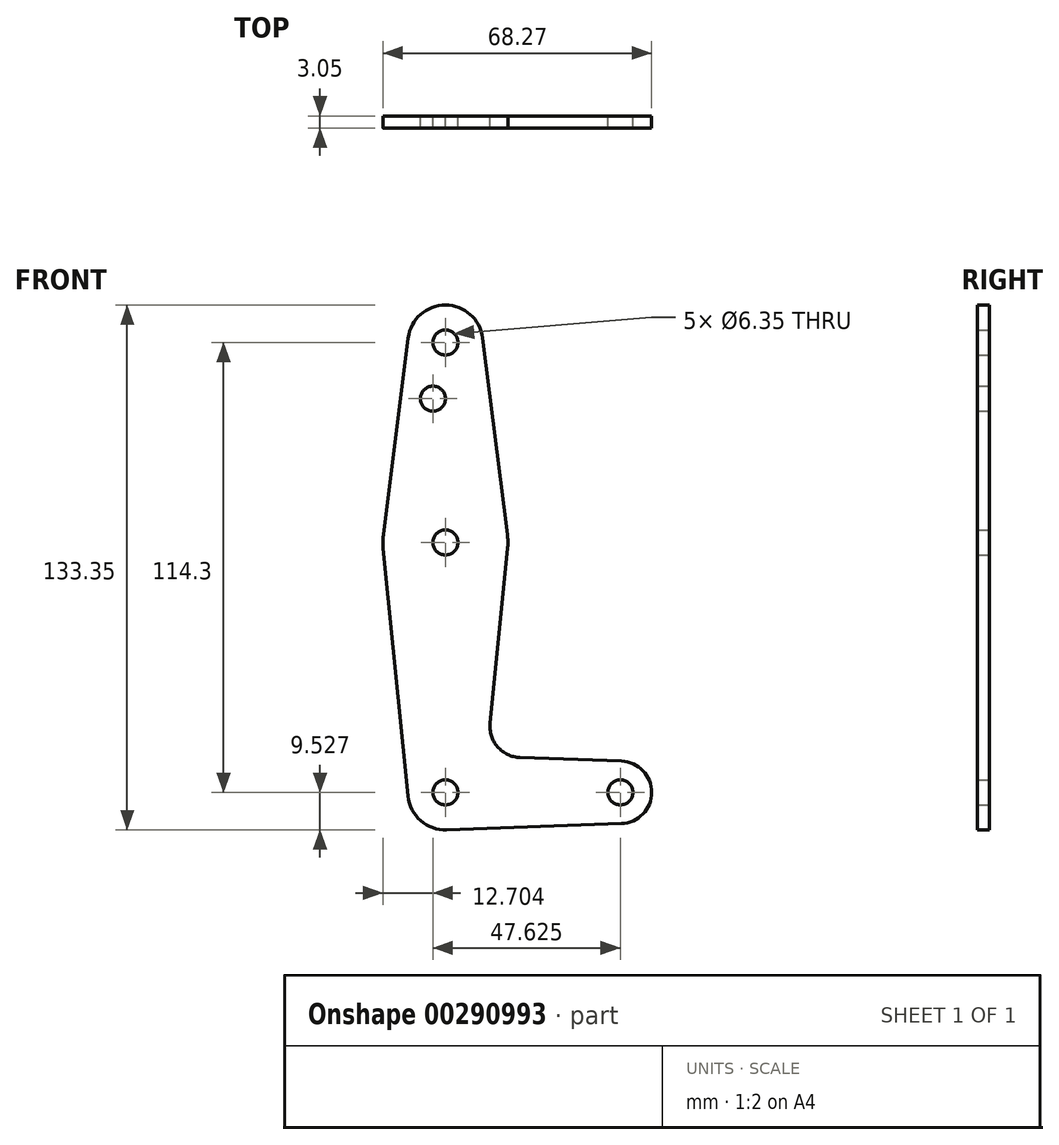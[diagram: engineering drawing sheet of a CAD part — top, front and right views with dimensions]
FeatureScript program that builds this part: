
annotation { "Feature Type Name" : "Feature", "Feature Type Description" : "" }
export const myFeature = defineFeature(function(context is Context, id is Id, definition is map)
    precondition{}
    {
        {
            var Q0;
            Q0=qCreatedBy(makeId("Front.planeOp"),FACE);
            var sketch = newSketch(context, id + "F0", { "sketchPlane" : qUnion([Q0])});
            skLineSegment(sketch, "E0", {"start": v(-31.57, 52.39) * mm, "end": v(-31.57, -61.91) * mm, "construction": true});
            skLineSegment(sketch, "E1", {"start": v(12.88, -61.91) * mm, "end": v(-31.57, -61.91) * mm});
            skCircle(sketch, "E2", {"center": v(-31.57, 52.39) * mm, "radius": 9.53 * mm});
            skCircle(sketch, "E3", {"center": v(-31.57, 1.59) * mm, "radius": 15.88 * mm});
            skCircle(sketch, "E4", {"center": v(-31.57, -61.91) * mm, "radius": 9.53 * mm});
            skCircle(sketch, "E5", {"center": v(12.88, -61.91) * mm, "radius": 7.94 * mm});
            skLineSegment(sketch, "E6", {"start": v(-47.32, 3.57) * mm, "end": v(-41.02, 53.58) * mm});
            skLineSegment(sketch, "E7", {"start": v(-15.82, 3.57) * mm, "end": v(-22.12, 53.58) * mm});
            skLineSegment(sketch, "E8", {"start": v(-47.37, 0) * mm, "end": v(-41.05, -62.87) * mm});
            skLineSegment(sketch, "E9", {"start": v(-15.78, 0) * mm, "end": v(-20.23, -44.32) * mm});
            skLineSegment(sketch, "E10", {"start": v(-12.6, -53.06) * mm, "end": v(13.16, -53.98) * mm});
            skLineSegment(sketch, "E11", {"start": v(13.16, -69.84) * mm, "end": v(-31.57, -71.44) * mm});
            skCircle(sketch, "E12", {"center": v(-31.57, 52.39) * mm, "radius": 3.18 * mm});
            skCircle(sketch, "E13", {"center": v(-34.75, 38.11) * mm, "radius": 3.18 * mm});
            skCircle(sketch, "E14", {"center": v(-31.57, 1.59) * mm, "radius": 3.18 * mm});
            skCircle(sketch, "E15", {"center": v(-31.57, -61.91) * mm, "radius": 3.18 * mm});
            skCircle(sketch, "E16", {"center": v(12.88, -61.91) * mm, "radius": 3.18 * mm});
            skPoint(sketch, "E17.newPointB", {"position": v(-31.57, -52.39) * mm});
            skArc(sketch, "E17.filletArc", {"start": v(-20.23, -44.32) * mm, "mid": v(-18.3, -50.35) * mm, "end": v(-12.6, -53.06) * mm});
            skSolve(sketch);
        }
        {
            var Q0;
            {var subQ1=sQuery(id+"F0.wireOp",EDGE,"E6");Q0=makeQuery(id+"F0.imprint","IMPRINT",FACE,{"disambiguationData":[TD([[makeQuery(id+"F0.imprint","IMPRINT",EDGE,{"derivedFrom":subQ1}),-1.0]])]});}
            var Q1;
            Q1=makeQuery(id+"F0.imprint","IMPRINT",FACE,{"disambiguationData":[TD([[makeQuery(id+"F0.imprint","IMPRINT",EDGE,{"derivedFrom":sQuery(id+"F0.wireOp",EDGE,"E12")}),-1.0]])]});
            var Q2;
            Q2=makeQuery(id+"F0.imprint","IMPRINT",FACE,{"disambiguationData":[TD([[makeQuery(id+"F0.imprint","IMPRINT",EDGE,{"derivedFrom":sQuery(id+"F0.wireOp",EDGE,"E14")}),-1.0]])]});
            var Q3;
            {var subQ0=sQuery(id+"F0.wireOp",EDGE,"E8");Q3=makeQuery(id+"F0.imprint","IMPRINT",FACE,{"disambiguationData":[TD([[makeQuery(id+"F0.imprint","IMPRINT",EDGE,{"derivedFrom":subQ0}),1.0]])]});}
            var Q4;
            Q4=makeQuery(id+"F0.imprint","IMPRINT",FACE,{"disambiguationData":[TD([[makeQuery(id+"F0.imprint","IMPRINT",EDGE,{"derivedFrom":sQuery(id+"F0.wireOp",EDGE,"E15")}),-1.0]])]});
            var Q5;
            {var subQ0=sQuery(id+"F0.wireOp",EDGE,"E4");var subQ1=sQuery(id+"F0.wireOp",EDGE,"E1");var subQ2=makeQuery(id+"F0.imprint","INTERSECT",VERTEX,{"derivedFrom":[subQ1,subQ0]});Q5=makeQuery(id+"F0.imprint","IMPRINT",FACE,{"disambiguationData":[TD([[makeQuery(id+"F0.imprint","IMPRINT",EDGE,{"disambiguationData":[TD([[subQ2,1.0]])],"derivedFrom":subQ1}),1.0]])]});}
            var Q6;
            Q6=makeQuery(id+"F0.imprint","IMPRINT",FACE,{"disambiguationData":[TD([[makeQuery(id+"F0.imprint","IMPRINT",EDGE,{"derivedFrom":sQuery(id+"F0.wireOp",EDGE,"E16")}),-1.0]])]});
            extrude(context, id + "F1", {"entities" : qUnion([Q0, Q1, Q2, Q3, Q4, Q5, Q6]), "depth" : 3.05 * mm});
        }
    });
